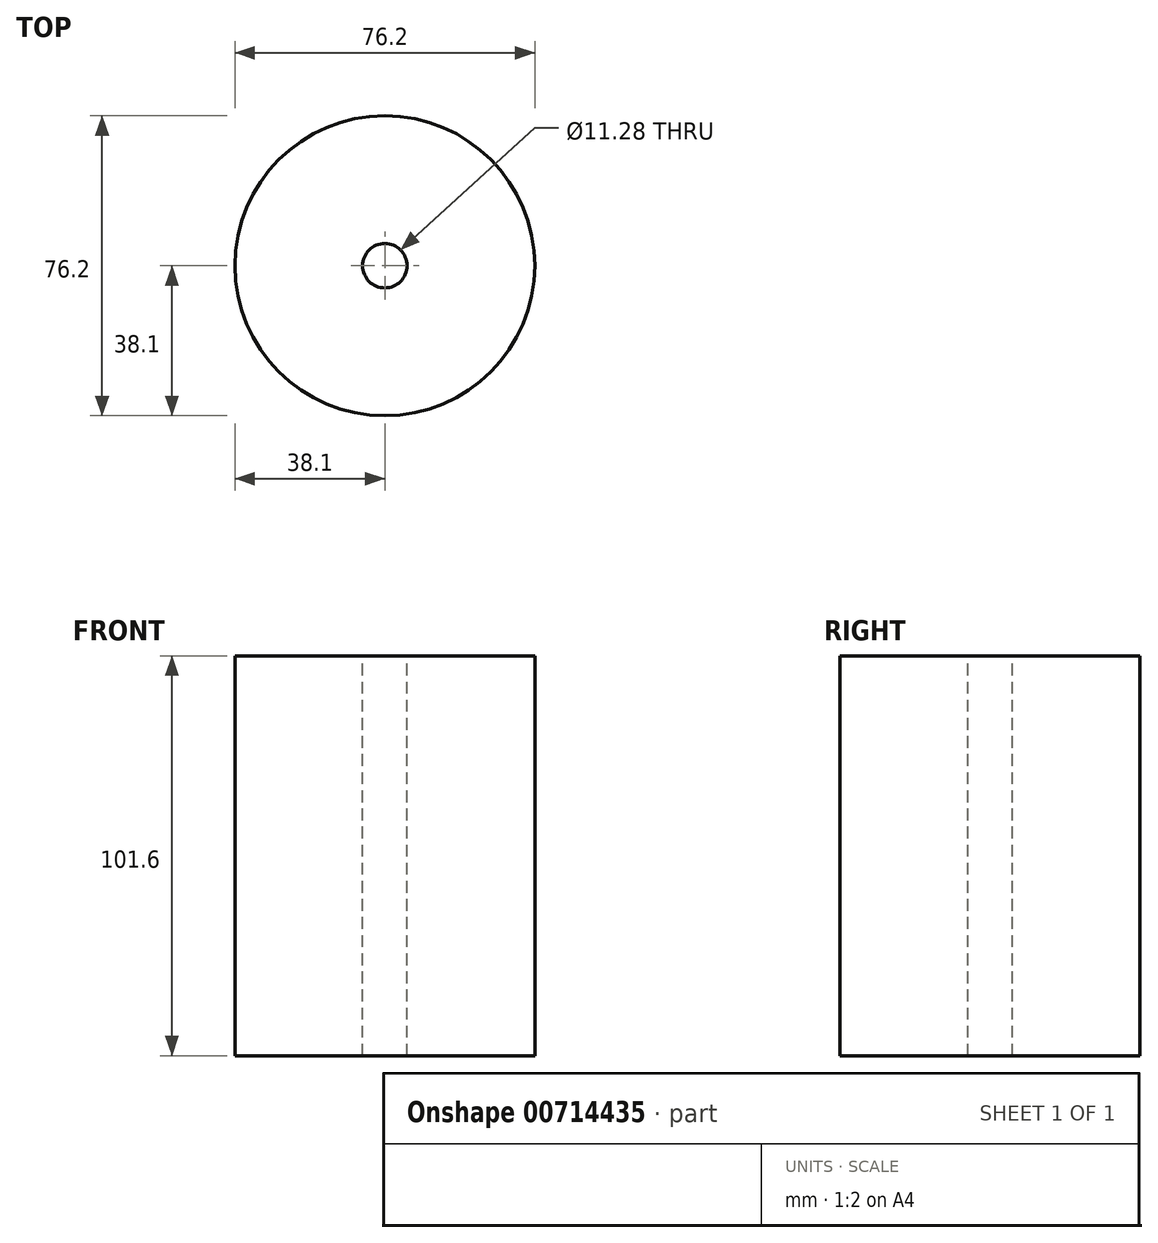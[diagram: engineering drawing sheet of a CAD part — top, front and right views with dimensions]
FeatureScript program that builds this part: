
annotation { "Feature Type Name" : "Feature", "Feature Type Description" : "" }
export const myFeature = defineFeature(function(context is Context, id is Id, definition is map)
    precondition{}
    {
        {
            var Q0;
            Q0=qCreatedBy(makeId("Top.planeOp"),FACE);
            var sketch = newSketch(context, id + "F0", { "sketchPlane" : qUnion([Q0])});
            skCircle(sketch, "E0", {"center": v(0, 0) * mm, "radius": 38.1 * mm});
            skCircle(sketch, "E1", {"center": v(0, 0) * mm, "radius": 5.64 * mm});
            skSolve(sketch);
        }
        {
            var Q0;
            Q0=qSketchRegion(id+"F0",true);
            extrude(context, id + "F1", {"entities" : qUnion([Q0]), "oppositeDirection" : true, "depth" : 101.6 * mm});
        }
    });
